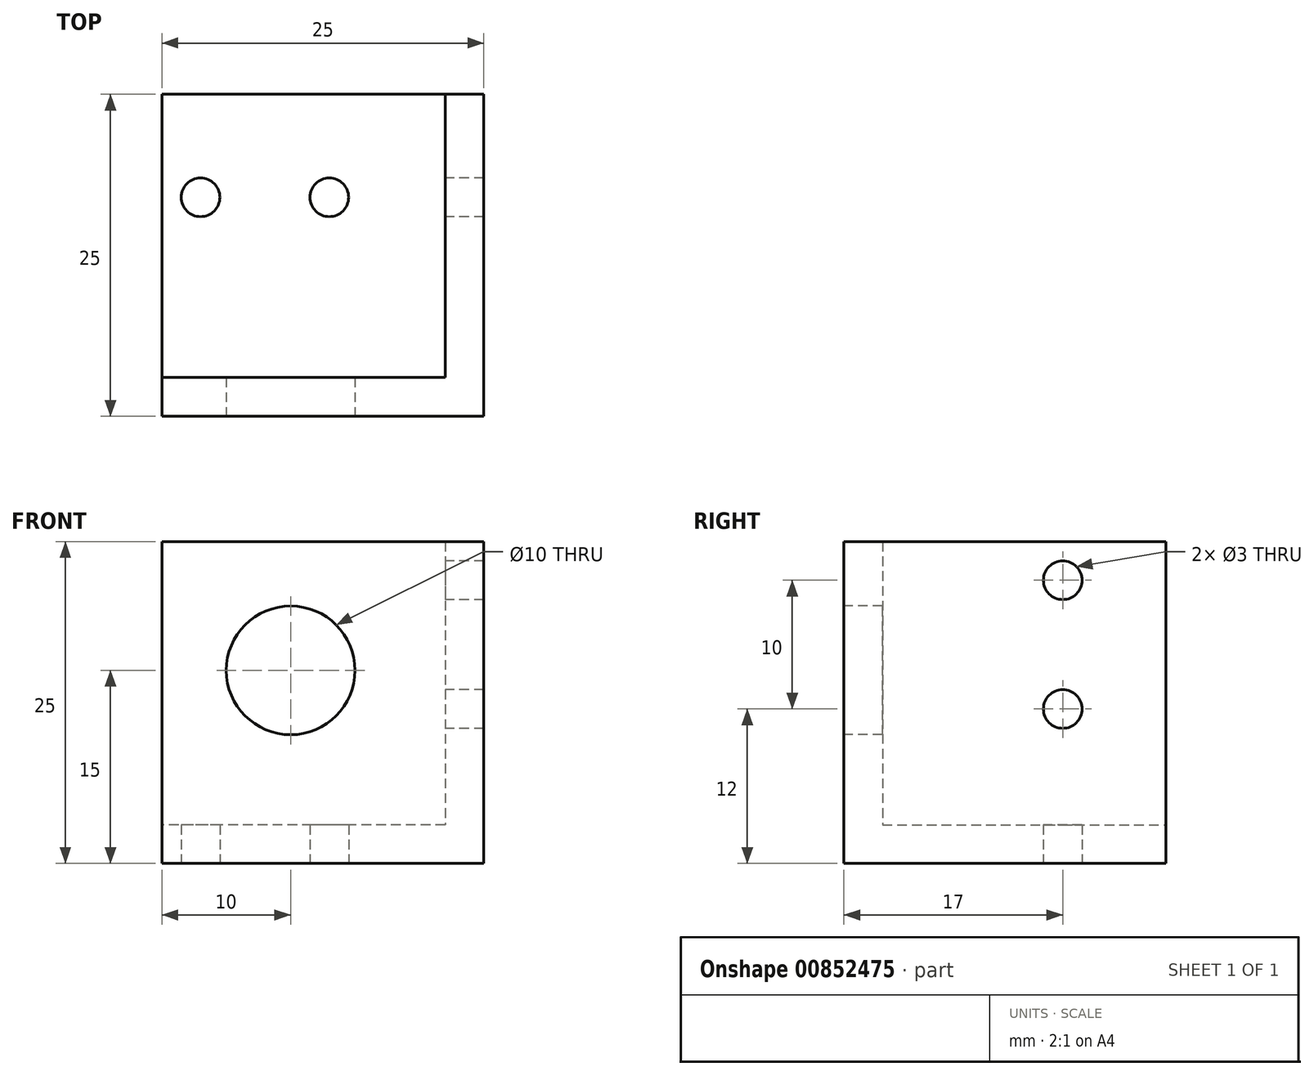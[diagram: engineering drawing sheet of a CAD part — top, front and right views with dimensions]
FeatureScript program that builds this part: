
annotation { "Feature Type Name" : "Feature", "Feature Type Description" : "" }
export const myFeature = defineFeature(function(context is Context, id is Id, definition is map)
    precondition{}
    {
        {
            var Q0;
            Q0=qCreatedBy(makeId("Top.planeOp"),FACE);
            var sketch = newSketch(context, id + "F0", { "sketchPlane" : qUnion([Q0])});
            skLineSegment(sketch, "E0.bottom", {"start": v(15, -17) * mm, "end": v(-10, -17) * mm});
            skLineSegment(sketch, "E0.top", {"start": v(15, 8) * mm, "end": v(-10, 8) * mm});
            skLineSegment(sketch, "E0.left", {"start": v(15, -17) * mm, "end": v(15, 8) * mm});
            skLineSegment(sketch, "E0.right", {"start": v(-10, -17) * mm, "end": v(-10, 8) * mm});
            skPoint(sketch, "E0.middle", {"position": v(0, 0) * mm});
            skLineSegment(sketch, "E1", {"start": v(0, 0) * mm, "end": v(0, 0) * mm});
            skLineSegment(sketch, "E2", {"start": v(0, 0) * mm, "end": v(3, 0) * mm});
            skLineSegment(sketch, "E3", {"start": v(0, 0) * mm, "end": v(-7, 0) * mm});
            skCircle(sketch, "E4", {"center": v(-7, 0) * mm, "radius": 1.5 * mm});
            skCircle(sketch, "E5", {"center": v(3, 0) * mm, "radius": 1.5 * mm});
            skSolve(sketch);
        }
        {
            var Q0;
            Q0=makeQuery(id+"F0.imprint","IMPRINT",FACE,{"disambiguationData":[TD([[makeQuery(id+"F0.imprint","IMPRINT",EDGE,{"derivedFrom":sQuery(id+"F0.wireOp",EDGE,"E0.bottom")}),-1.0]])]});
            extrude(context, id + "F1", {"entities" : qUnion([Q0]), "depth" : 3 * mm, "offsetDistance" : 25 * mm});
        }
        {
            var Q0;
            Q0=makeQuery(id+"F0.imprint","IMPRINT",FACE,{"disambiguationData":[TD([[makeQuery(id+"F0.imprint","IMPRINT",EDGE,{"derivedFrom":sQuery(id+"F0.wireOp",EDGE,"E0.bottom")}),-1.0]])]});
            extrude(context, id + "F2", {"entities" : qUnion([Q0]), "operationType" : NewBodyOperationType.ADD, "depth" : 3 * mm, "offsetDistance" : 25 * mm});
        }
        {
            var Q0;
            Q0=makeQuery(id+"F1.opExtrude","CAP_FACE",FACE,{"disambiguationData":[OSD([sQuery(id+"F0.wireOp",EDGE,"E0.bottom"),sQuery(id+"F0.wireOp",EDGE,"E0.top"),sQuery(id+"F0.wireOp",EDGE,"E0.left"),sQuery(id+"F0.wireOp",EDGE,"E0.right"),sQuery(id+"F0.wireOp",EDGE,"E4"),sQuery(id+"F0.wireOp",EDGE,"E5")])],"isStart":false});
            var sketch = newSketch(context, id + "F3", { "sketchPlane" : qUnion([Q0])});
            skLineSegment(sketch, "E6.bottom", {"start": v(15, -17) * mm, "end": v(-10, -17) * mm});
            skLineSegment(sketch, "E6.top", {"start": v(15, -14) * mm, "end": v(-10, -14) * mm});
            skLineSegment(sketch, "E6.left", {"start": v(15, -17) * mm, "end": v(15, -14) * mm});
            skLineSegment(sketch, "E6.right", {"start": v(-10, -17) * mm, "end": v(-10, -14) * mm});
            skSolve(sketch);
        }
        {
            var Q0;
            Q0 = qSketchRegion(id + "F3", true);
            extrude(context, id + "F4", {"entities" : qUnion([Q0]), "operationType" : NewBodyOperationType.ADD, "depth" : 22 * mm, "offsetDistance" : 25 * mm});
        }
        {
            var Q0;
            Q0=makeQuery(id+"F4.opExtrude","SWEPT_FACE",FACE,{"disambiguationData":[OSD([sQuery(id+"F3.wireOp",EDGE,"E6.top")])]});
            var sketch = newSketch(context, id + "F5", { "sketchPlane" : qUnion([Q0])});
            skLineSegment(sketch, "E7.bottom", {"start": v(-15, 25) * mm, "end": v(-12, 25) * mm});
            skLineSegment(sketch, "E7.top", {"start": v(-15, 3) * mm, "end": v(-12, 3) * mm});
            skLineSegment(sketch, "E7.left", {"start": v(-15, 25) * mm, "end": v(-15, 3) * mm});
            skLineSegment(sketch, "E7.right", {"start": v(-12, 25) * mm, "end": v(-12, 3) * mm});
            skSolve(sketch);
        }
        {
            var Q0;
            Q0 = qSketchRegion(id + "F5", true);
            extrude(context, id + "F6", {"entities" : qUnion([Q0]), "operationType" : NewBodyOperationType.ADD, "depth" : 22 * mm, "offsetDistance" : 25 * mm});
        }
        {
            var Q0;
            Q0=makeQuery(id+"F6.opExtrude","SWEPT_FACE",FACE,{"disambiguationData":[OSD([sQuery(id+"F5.wireOp",EDGE,"E7.right")])]});
            var sketch = newSketch(context, id + "F7", { "sketchPlane" : qUnion([Q0])});
            skCircle(sketch, "E8", {"center": v(0, 22) * mm, "radius": 1.5 * mm});
            skCircle(sketch, "E9", {"center": v(0, 12) * mm, "radius": 1.5 * mm});
            skLineSegment(sketch, "E10", {"start": v(0, 22) * mm, "end": v(0, 25) * mm});
            skLineSegment(sketch, "E11", {"start": v(0, 12) * mm, "end": v(0, 22) * mm});
            skSolve(sketch);
        }
        {
            var Q0;
            Q0=makeQuery(id+"F7.imprint","IMPRINT",FACE,{"disambiguationData":[TD([[makeQuery(id+"F7.imprint","IMPRINT",EDGE,{"derivedFrom":sQuery(id+"F7.wireOp",EDGE,"E9")}),1.0]])]});
            var Q1;
            {var subQ0=sQuery(id+"F7.wireOp",EDGE,"E10");var subQ1=sQuery(id+"F7.wireOp",EDGE,"E8");var subQ2=makeQuery(id+"F7.imprint","INTERSECT",VERTEX,{"derivedFrom":[subQ1,subQ0]});Q1=makeQuery(id+"F7.imprint","IMPRINT",FACE,{"disambiguationData":[TD([[makeQuery(id+"F7.imprint","IMPRINT",EDGE,{"disambiguationData":[TD([[subQ2,1.0]])],"derivedFrom":subQ1}),1.0]])]});}
            var Q2;
            {var subQ0=sQuery(id+"F7.wireOp",EDGE,"E10");var subQ1=sQuery(id+"F7.wireOp",EDGE,"E8");var subQ2=makeQuery(id+"F7.imprint","INTERSECT",VERTEX,{"derivedFrom":[subQ1,subQ0]});Q2=makeQuery(id+"F7.imprint","IMPRINT",FACE,{"disambiguationData":[TD([[makeQuery(id+"F7.imprint","IMPRINT",EDGE,{"disambiguationData":[TD([[subQ2,-1.0]])],"derivedFrom":subQ1}),1.0]])]});}
            var Q3;
            Q3=sQuery(id+"F7.wireOp",EDGE,"E9");
            var Q4;
            Q4=sQuery(id+"F7.wireOp",EDGE,"E8");
            extrude(context, id + "F8", {"entities" : qUnion([Q0, Q1, Q2]), "operationType" : NewBodyOperationType.REMOVE, "surfaceEntities" : qUnion([Q3, Q4]), "oppositeDirection" : true, "depth" : 25 * mm, "offsetDistance" : 25 * mm});
        }
        {
            var Q0;
            Q0=makeQuery(id+"F4.boolean.opBoolean","MERGE",FACE,{"derivedFrom":[makeQuery(id+"F1.opExtrude","SWEPT_FACE",FACE,{"disambiguationData":[OSD([sQuery(id+"F0.wireOp",EDGE,"E0.bottom")])]}),makeQuery(id+"F4.opExtrude","SWEPT_FACE",FACE,{"disambiguationData":[OSD([sQuery(id+"F3.wireOp",EDGE,"E6.bottom")])]})]});
            var sketch = newSketch(context, id + "F9", { "sketchPlane" : qUnion([Q0])});
            skCircle(sketch, "E12", {"center": v(0, 15) * mm, "radius": 5 * mm});
            skSolve(sketch);
        }
        {
            var Q0;
            Q0=makeQuery(id+"F9.imprint","IMPRINT",FACE,{"disambiguationData":[TD([[makeQuery(id+"F9.imprint","IMPRINT",EDGE,{"derivedFrom":sQuery(id+"F9.wireOp",EDGE,"E12")}),1.0]])]});
            extrude(context, id + "F10", {"entities" : qUnion([Q0]), "operationType" : NewBodyOperationType.REMOVE, "oppositeDirection" : true, "depth" : 25 * mm, "offsetDistance" : 25 * mm});
        }
    });
